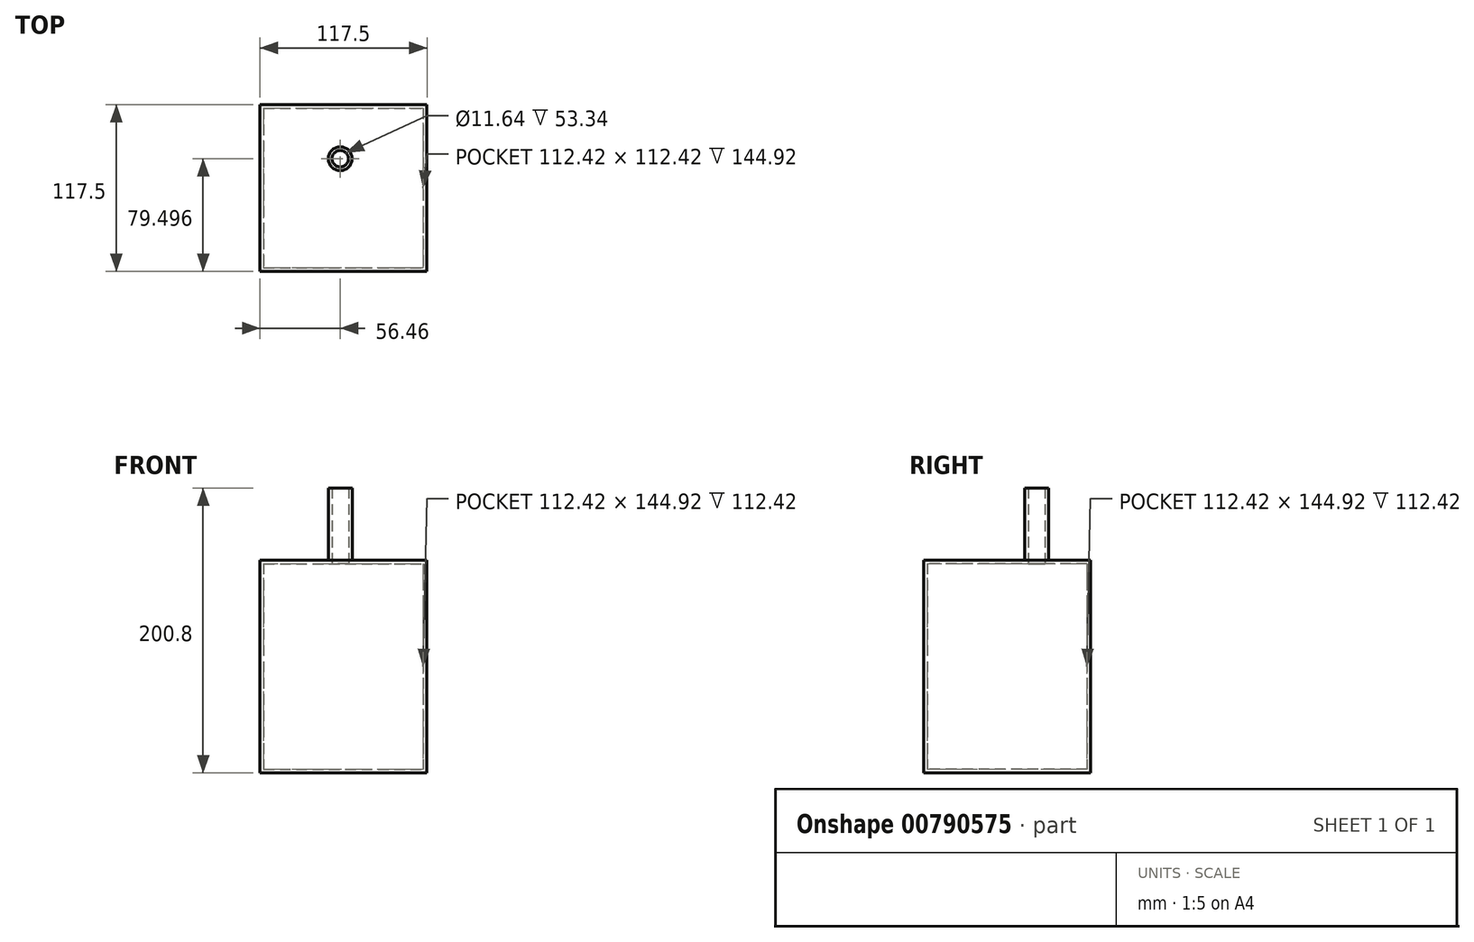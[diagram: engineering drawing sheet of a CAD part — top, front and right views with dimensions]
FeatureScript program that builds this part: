
annotation { "Feature Type Name" : "Feature", "Feature Type Description" : "" }
export const myFeature = defineFeature(function(context is Context, id is Id, definition is map)
    precondition{}
    {
        {
            var Q0;
            Q0=qCreatedBy(makeId("Top.planeOp"),FACE);
            var sketch = newSketch(context, id + "F0", { "sketchPlane" : qUnion([Q0])});
            skLineSegment(sketch, "E0.bottom", {"start": v(-56.46, 48.8) * mm, "end": v(61.04, 48.8) * mm});
            skLineSegment(sketch, "E0.top", {"start": v(-56.46, -68.7) * mm, "end": v(61.04, -68.7) * mm});
            skLineSegment(sketch, "E0.left", {"start": v(-56.46, 48.8) * mm, "end": v(-56.46, -68.7) * mm});
            skLineSegment(sketch, "E0.right", {"start": v(61.04, 48.8) * mm, "end": v(61.04, -68.7) * mm});
            skSolve(sketch);
        }
        {
            var Q0;
            Q0 = qSketchRegion(id + "F0", true);
            extrude(context, id + "F1", {"entities" : qUnion([Q0]), "depth" : 150 * mm, "offsetDistance" : 25.4 * mm});
        }
        {
            var Q0;
            Q0=makeQuery(id+"F1.opExtrude","CAP_FACE",FACE,{"disambiguationData":[OSD([sQuery(id+"F0.wireOp",EDGE,"E0.bottom"),sQuery(id+"F0.wireOp",EDGE,"E0.top"),sQuery(id+"F0.wireOp",EDGE,"E0.left"),sQuery(id+"F0.wireOp",EDGE,"E0.right")])],"isStart":false});
            var sketch = newSketch(context, id + "F2", { "sketchPlane" : qUnion([Q0])});
            skCircle(sketch, "E1", {"center": v(0, 10.8) * mm, "radius": 8.36 * mm});
            skSolve(sketch);
        }
        {
            var Q0;
            Q0=makeQuery(id+"F2.imprint","IMPRINT",FACE,{"disambiguationData":[TD([[makeQuery(id+"F2.imprint","IMPRINT",EDGE,{"derivedFrom":sQuery(id+"F2.wireOp",EDGE,"E1")}),1.0]])]});
            extrude(context, id + "F3", {"entities" : qUnion([Q0]), "operationType" : NewBodyOperationType.ADD, "depth" : 50.8 * mm, "offsetDistance" : 25.4 * mm});
        }
        {
            var Q0;
            Q0=makeQuery(id+"F3.opExtrude","CAP_FACE",FACE,{"disambiguationData":[OSD([sQuery(id+"F2.wireOp",EDGE,"E1")])],"isStart":false});
            shell(context, id + "F4", {"entities" : qUnion([Q0]), "thickness" : 2.54 * mm});
        }
    });
